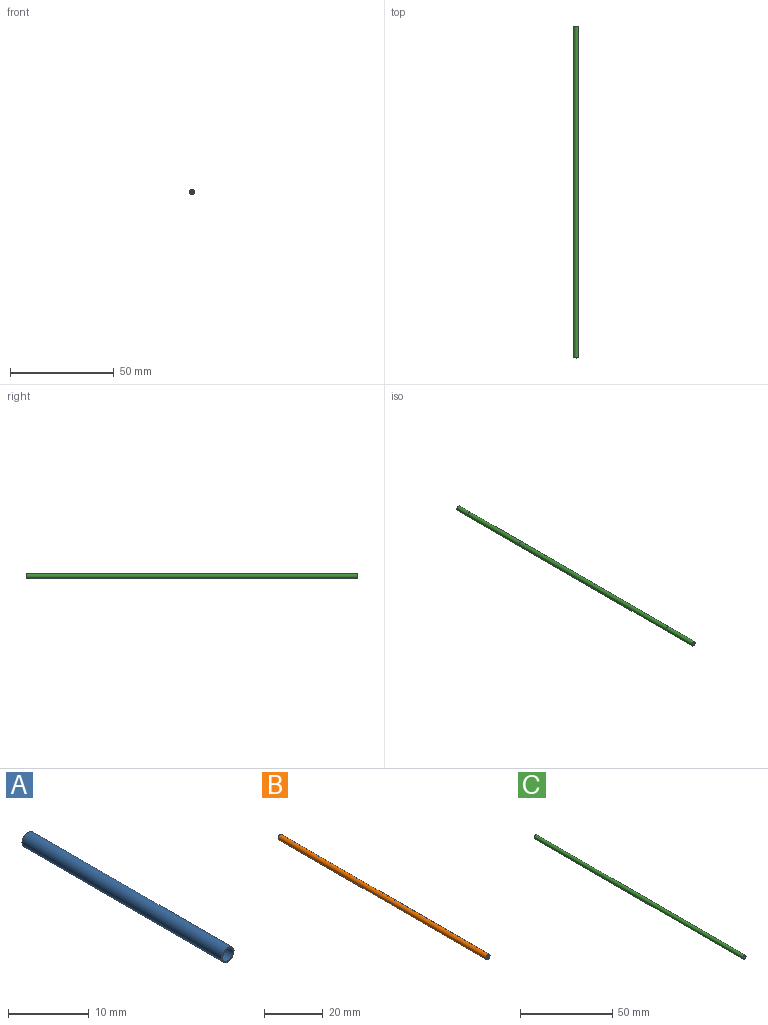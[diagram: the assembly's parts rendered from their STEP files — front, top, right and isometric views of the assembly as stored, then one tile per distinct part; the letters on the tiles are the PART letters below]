
ASSEMBLY  parts=3 mates=2
PART A: 4 faces, bbox 2.2x35x2.2 mm
  f0: cylinder r=0.93mm len=35mm, axis (0,1,0), area 203.4mm2, adj f2,f3
  f1: cylinder r=1.07mm len=35mm, axis (0,1,0), area 236.4mm2, adj f2,f3
  f2: plane 2.15x2.15mm, normal (0,-1,0), area 0.9mm2, adj f0,f1
  f3: plane 2.15x2.15mm, normal (0,1,0), area 0.9mm2, adj f0,f1
PART B: 7 faces, bbox 2.1x100x2.1 mm
  f0: cylinder r=0.3mm len=100mm, axis (0,1,0), area 188.5mm2, adj f5,f6
  f1: cylinder r=0.17mm len=100mm, axis (0,1,0), area 110mm2, adj f5,f6
  f2: cylinder r=0.5mm len=100mm, axis (0,1,0), area 314.2mm2, adj f5,f6
  f3: cylinder r=0.17mm len=100mm, axis (0,1,0), area 110mm2, adj f5,f6
  f4: cylinder r=1.03mm len=100mm, axis (0,1,0), area 644mm2, adj f5,f6
  f5: plane 2.05x2.05mm, normal (0,-1,0), area 2mm2, adj f0,f1,f2,f3,f4
  f6: plane 2.05x2.05mm, normal (0,1,0), area 2mm2, adj f0,f1,f2,f3,f4
PART C: 4 faces, bbox 2.4x160x2.4 mm
  f0: cylinder r=0.8mm len=160mm, axis (0,1,0), area 804.2mm2, adj f2,f3
  f1: cylinder r=1.2mm len=160mm, axis (0,1,0), area 1206.4mm2, adj f2,f3
  f2: plane 2.4x2.4mm, normal (0,-1,0), area 2.5mm2, adj f0,f1
  f3: plane 2.4x2.4mm, normal (0,1,0), area 2.5mm2, adj f0,f1
PLACE A t=(-10.53,5.77,-9.2)mm
PLACE B t=(80.43,-29.36,-34.99)mm
PLACE C t=(-10.53,13.03,-9.2)mm
MATE slider A.f1 <-> C.f0  axis (0,1,0) through (-10.53,5.77,-9.2)mm
MATE slider B.f4 <-> C.f1  axis (0,1,0) through (-10.53,-79.36,-9.2)mm
